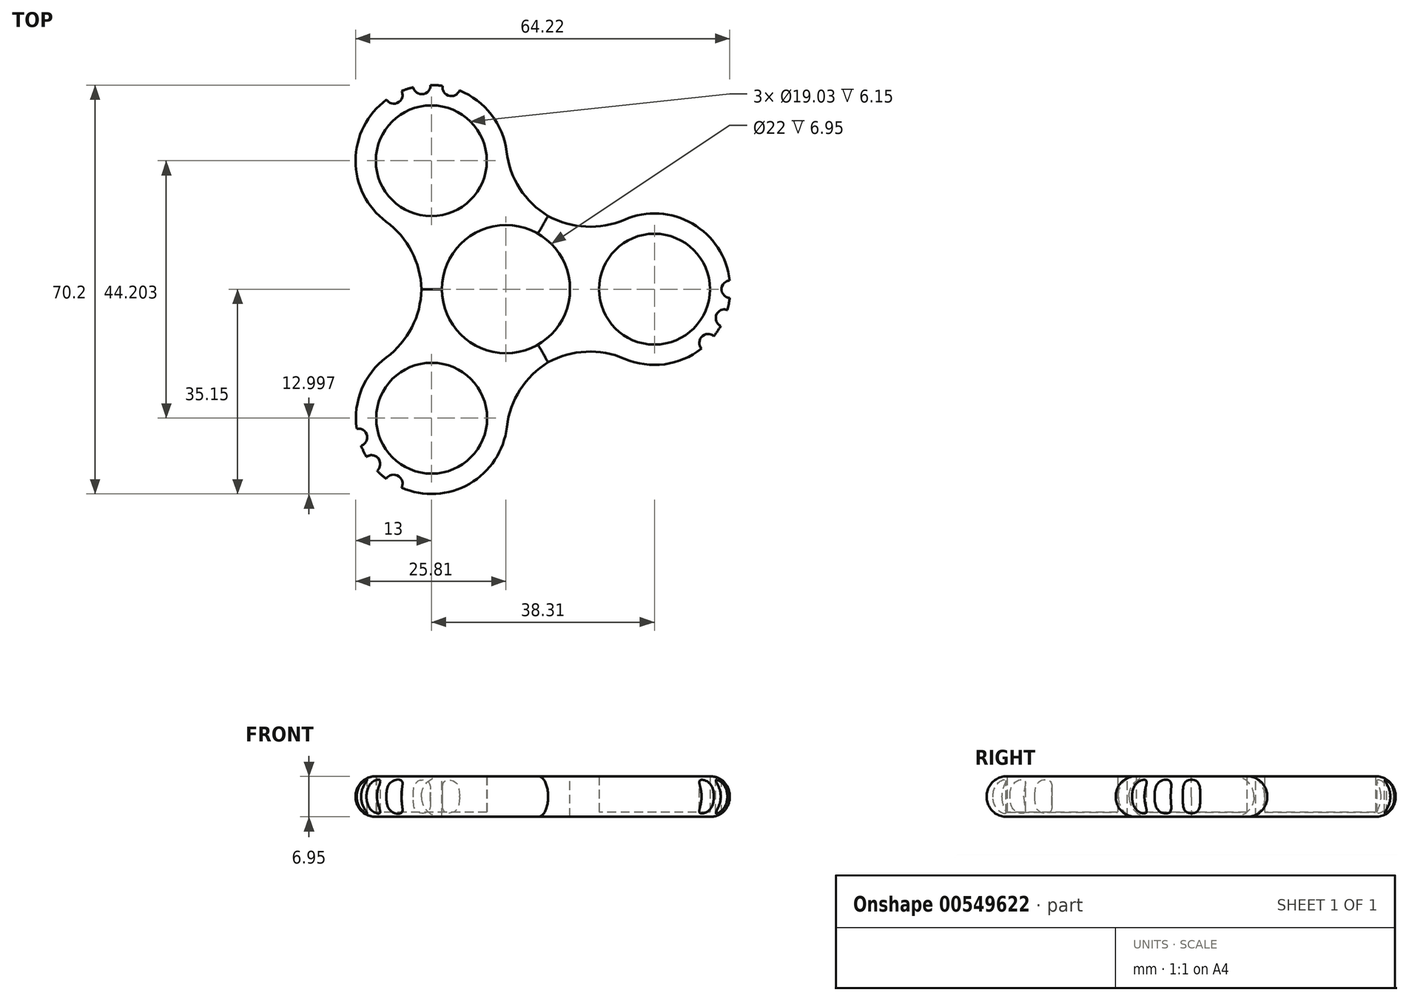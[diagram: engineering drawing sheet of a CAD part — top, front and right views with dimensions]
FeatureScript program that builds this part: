
annotation { "Feature Type Name" : "Feature", "Feature Type Description" : "" }
export const myFeature = defineFeature(function(context is Context, id is Id, definition is map)
    precondition{}
    {
        {
            var Q0;
            Q0=qCreatedBy(makeId("Top.planeOp"),FACE);
            var sketch = newSketch(context, id + "F0", { "sketchPlane" : qUnion([Q0])});
            skArc(sketch, "E0", {"start": v(13.56, -5.14) * mm, "mid": v(38.5, 0) * mm, "end": v(13.56, 5.14) * mm});
            skCircle(sketch, "E1", {"center": v(0, 0) * mm, "radius": 11 * mm});
            skCircle(sketch, "E2", {"center": v(25.5, 0) * mm, "radius": 9.52 * mm});
            skArc(sketch, "E3.1.1", {"start": v(-2.37, 14.3) * mm, "mid": v(-19.34, 33.3) * mm, "end": v(-11.25, 9.14) * mm});
            skCircle(sketch, "E3.1.2", {"center": v(-12.81, 22.05) * mm, "radius": 9.52 * mm});
            skArc(sketch, "E3.2.1", {"start": v(-11.17, -9.25) * mm, "mid": v(-19.24, -33.42) * mm, "end": v(-2.39, -14.3) * mm});
            skCircle(sketch, "E3.2.2", {"center": v(-12.75, -22.15) * mm, "radius": 9.52 * mm});
            skPoint(sketch, "E3.center", {"position": v(-0.02, -0.03) * mm});
            skArc(sketch, "E4", {"start": v(-11.25, 9.14) * mm, "mid": v(-14.5, -0.07) * mm, "end": v(-11.17, -9.25) * mm});
            skArc(sketch, "E5.trimOffspring", {"start": v(-2.39, -14.3) * mm, "mid": v(7.22, -12.57) * mm, "end": v(13.56, -5.14) * mm});
            skArc(sketch, "E6.trimOffspring", {"start": v(13.56, 5.14) * mm, "mid": v(7.23, 12.57) * mm, "end": v(-2.37, 14.3) * mm});
            skSolve(sketch);
        }
        {
            var Q0;
            Q0=makeQuery(id+"F0.imprint","IMPRINT",FACE,{"disambiguationData":[TD([[makeQuery(id+"F0.imprint","IMPRINT",EDGE,{"derivedFrom":sQuery(id+"F0.wireOp",EDGE,"E3.1.2")}),-1.0]])]});
            var Q1;
            {var subQ7=sQuery(id+"F0.wireOp",EDGE,"s7jpMl1W-r8wG-a5Qh-Sgcx-P4qn6cR7i1xz");var subQ8=sQuery(id+"F0.wireOp",EDGE,"E1");var subQ9=makeQuery(id+"F0.imprint","INTERSECT",VERTEX,{"derivedFrom":[subQ8,subQ7]});Q1=makeQuery(id+"F0.imprint","IMPRINT",FACE,{"disambiguationData":[TD([[makeQuery(id+"F0.imprint","IMPRINT",EDGE,{"disambiguationData":[TD([[subQ9,-1.0]])],"derivedFrom":subQ8}),-1.0]])]});}
            var Q2;
            {var subQ0=sQuery(id+"F0.wireOp",EDGE,"E1");var subQ4=makeQuery(id+"F0.imprint","INTERSECT",VERTEX,{"derivedFrom":[subQ0,sQuery(id+"F0.wireOp",EDGE,"s7jpMl1W-r8wG-a5Qh-Sgcx-P4qn6cR7i1xz")]});Q2=makeQuery(id+"F0.imprint","IMPRINT",FACE,{"disambiguationData":[TD([[makeQuery(id+"F0.imprint","IMPRINT",EDGE,{"disambiguationData":[TD([[subQ4,1.0]])],"derivedFrom":subQ0}),1.0]])]});}
            var Q3;
            {var subQ0=sQuery(id+"F0.wireOp",EDGE,"s7jpMl1W-r8wG-a5Qh-Sgcx-P4qn6cR7i1xz");var subQ1=sQuery(id+"F0.wireOp",EDGE,"E1");var subQ2=makeQuery(id+"F0.imprint","INTERSECT",VERTEX,{"derivedFrom":[subQ1,subQ0]});Q3=makeQuery(id+"F0.imprint","IMPRINT",FACE,{"disambiguationData":[TD([[makeQuery(id+"F0.imprint","IMPRINT",EDGE,{"disambiguationData":[TD([[subQ2,1.0]])],"derivedFrom":subQ1}),-1.0]])]});}
            var Q4;
            {var subQ1=sQuery(id+"F0.wireOp",EDGE,"E0");var subQ5=sQuery(id+"F0.wireOp",EDGE,"s7jpMl1W-r8wG-a5Qh-Sgcx-P4qn6cR7i1xz");var subQ6=makeQuery(id+"F0.imprint","INTERSECT",VERTEX,{"derivedFrom":[subQ1,subQ5]});Q4=makeQuery(id+"F0.imprint","IMPRINT",FACE,{"disambiguationData":[TD([[makeQuery(id+"F0.imprint","IMPRINT",EDGE,{"disambiguationData":[TD([[subQ6,-1.0]])],"derivedFrom":subQ1}),-1.0]])]});}
            var Q5;
            Q5=makeQuery(id+"F0.imprint","IMPRINT",FACE,{"disambiguationData":[TD([[makeQuery(id+"F0.imprint","IMPRINT",EDGE,{"derivedFrom":sQuery(id+"F0.wireOp",EDGE,"E2")}),-1.0]])]});
            var Q6;
            {var subQ0=sQuery(id+"F0.wireOp",EDGE,"E3.1.0");var subQ1=sQuery(id+"F0.wireOp",EDGE,"E1");var subQ2=makeQuery(id+"F0.imprint","INTERSECT",VERTEX,{"derivedFrom":[subQ1,subQ0]});Q6=makeQuery(id+"F0.imprint","IMPRINT",FACE,{"disambiguationData":[TD([[makeQuery(id+"F0.imprint","IMPRINT",EDGE,{"disambiguationData":[TD([[subQ2,1.0]])],"derivedFrom":subQ1}),-1.0]])]});}
            var Q7;
            {var subQ0=sQuery(id+"F0.wireOp",EDGE,"oMTgFF3v-ILPk-WRDk-ok4o-FcpdyRUbkfb3");var subQ1=sQuery(id+"F0.wireOp",EDGE,"E1");var subQ2=makeQuery(id+"F0.imprint","INTERSECT",VERTEX,{"derivedFrom":[subQ1,subQ0]});Q7=makeQuery(id+"F0.imprint","IMPRINT",FACE,{"disambiguationData":[TD([[makeQuery(id+"F0.imprint","IMPRINT",EDGE,{"disambiguationData":[TD([[subQ2,-1.0]])],"derivedFrom":subQ1}),-1.0]])]});}
            var Q8;
            {var subQ3=sQuery(id+"F0.wireOp",EDGE,"oMTgFF3v-ILPk-WRDk-ok4o-FcpdyRUbkfb3");var subQ5=sQuery(id+"F0.wireOp",EDGE,"E1");var subQ6=makeQuery(id+"F0.imprint","INTERSECT",VERTEX,{"derivedFrom":[subQ5,subQ3]});Q8=makeQuery(id+"F0.imprint","IMPRINT",FACE,{"disambiguationData":[TD([[makeQuery(id+"F0.imprint","IMPRINT",EDGE,{"disambiguationData":[TD([[subQ6,1.0]])],"derivedFrom":subQ5}),-1.0]])]});}
            var Q9;
            Q9=makeQuery(id+"F0.imprint","IMPRINT",FACE,{"disambiguationData":[TD([[makeQuery(id+"F0.imprint","IMPRINT",EDGE,{"derivedFrom":sQuery(id+"F0.wireOp",EDGE,"E3.2.2")}),-1.0]])]});
            extrude(context, id + "F1", {"entities" : qUnion([Q0, Q1, Q2, Q3, Q4, Q5, Q6, Q7, Q8, Q9]), "depth" : 6.95 * mm, "offsetDistance" : 25 * mm});
        }
        {
            var Q0;
            Q0=makeQuery(id+"F1.opExtrude","SWEPT_EDGE",EDGE,{"disambiguationData":[OSD([sQuery(id+"F0.wireOp",EDGE,"E3.1.1"),sQuery(id+"F0.wireOp",EDGE,"E4")])]});
            var Q1;
            Q1=makeQuery(id+"F1.opExtrude","SWEPT_EDGE",EDGE,{"disambiguationData":[OSD([sQuery(id+"F0.wireOp",EDGE,"E3.2.1"),sQuery(id+"F0.wireOp",EDGE,"E4")])]});
            var Q2;
            Q2=makeQuery(id+"F1.opExtrude","SWEPT_EDGE",EDGE,{"disambiguationData":[OSD([sQuery(id+"F0.wireOp",EDGE,"E0"),sQuery(id+"F0.wireOp",EDGE,"E5.trimOffspring")])]});
            var Q3;
            Q3=makeQuery(id+"F1.opExtrude","SWEPT_EDGE",EDGE,{"disambiguationData":[OSD([sQuery(id+"F0.wireOp",EDGE,"E3.2.1"),sQuery(id+"F0.wireOp",EDGE,"E5.trimOffspring")])]});
            var Q4;
            Q4=makeQuery(id+"F1.opExtrude","SWEPT_EDGE",EDGE,{"disambiguationData":[OSD([sQuery(id+"F0.wireOp",EDGE,"E0"),sQuery(id+"F0.wireOp",EDGE,"E6.trimOffspring")])]});
            var Q5;
            Q5=makeQuery(id+"F1.opExtrude","SWEPT_EDGE",EDGE,{"disambiguationData":[OSD([sQuery(id+"F0.wireOp",EDGE,"E3.1.1"),sQuery(id+"F0.wireOp",EDGE,"E6.trimOffspring")])]});
            fillet(context, id + "F2", {"entities" : qUnion([Q0, Q1, Q2, Q3, Q4, Q5]), "radius" : 15 * mm, "tangentPropagation" : true, "allowEdgeOverflow" : false});
        }
        {
            var Q0;
            {var subQ0=sQuery(id+"F0.wireOp",EDGE,"E6.trimOffspring");var subQ1=sQuery(id+"F0.wireOp",EDGE,"E3.1.1");Q0=makeQuery(id+"F2.opFillet","BLEND_EDGE",EDGE,{"blendedFrom":[makeQuery(id+"F1.opExtrude","SWEPT_EDGE",EDGE,{"disambiguationData":[OSD([subQ1,subQ0])]}),makeQuery(id+"F1.opExtrude","CAP_FACE",FACE,{"disambiguationData":[OSD([sQuery(id+"F0.wireOp",EDGE,"E0"),sQuery(id+"F0.wireOp",EDGE,"E1"),sQuery(id+"F0.wireOp",EDGE,"E2"),subQ1,sQuery(id+"F0.wireOp",EDGE,"E3.1.2"),sQuery(id+"F0.wireOp",EDGE,"E3.2.1"),sQuery(id+"F0.wireOp",EDGE,"E3.2.2"),sQuery(id+"F0.wireOp",EDGE,"E4"),sQuery(id+"F0.wireOp",EDGE,"E5.trimOffspring"),subQ0])],"isStart":false})],"blendedInto":[makeQuery(id+"F1.opExtrude","CAP_FACE",FACE,{"disambiguationData":[OSD([sQuery(id+"F0.wireOp",EDGE,"E0"),sQuery(id+"F0.wireOp",EDGE,"E1"),sQuery(id+"F0.wireOp",EDGE,"E2"),subQ1,sQuery(id+"F0.wireOp",EDGE,"E3.1.2"),sQuery(id+"F0.wireOp",EDGE,"E3.2.1"),sQuery(id+"F0.wireOp",EDGE,"E3.2.2"),sQuery(id+"F0.wireOp",EDGE,"E4"),sQuery(id+"F0.wireOp",EDGE,"E5.trimOffspring"),subQ0])],"isStart":false})]});}
            var Q1;
            Q1=makeQuery(id+"F1.opExtrude","CAP_EDGE",EDGE,{"disambiguationData":[OSD([sQuery(id+"F0.wireOp",EDGE,"E0")])],"isStart":false});
            var Q2;
            Q2=makeQuery(id+"F1.opExtrude","CAP_EDGE",EDGE,{"disambiguationData":[OSD([sQuery(id+"F0.wireOp",EDGE,"E3.2.1")])],"isStart":false});
            var Q3;
            {var subQ0=sQuery(id+"F0.wireOp",EDGE,"E6.trimOffspring");var subQ1=sQuery(id+"F0.wireOp",EDGE,"E3.1.1");Q3=makeQuery(id+"F2.opFillet","BLEND_EDGE",EDGE,{"blendedFrom":[makeQuery(id+"F1.opExtrude","SWEPT_EDGE",EDGE,{"disambiguationData":[OSD([subQ1,subQ0])]}),makeQuery(id+"F1.opExtrude","CAP_FACE",FACE,{"disambiguationData":[OSD([sQuery(id+"F0.wireOp",EDGE,"E0"),sQuery(id+"F0.wireOp",EDGE,"E1"),sQuery(id+"F0.wireOp",EDGE,"E2"),subQ1,sQuery(id+"F0.wireOp",EDGE,"E3.1.2"),sQuery(id+"F0.wireOp",EDGE,"E3.2.1"),sQuery(id+"F0.wireOp",EDGE,"E3.2.2"),sQuery(id+"F0.wireOp",EDGE,"E4"),sQuery(id+"F0.wireOp",EDGE,"E5.trimOffspring"),subQ0])],"isStart":true})],"blendedInto":[makeQuery(id+"F1.opExtrude","CAP_FACE",FACE,{"disambiguationData":[OSD([sQuery(id+"F0.wireOp",EDGE,"E0"),sQuery(id+"F0.wireOp",EDGE,"E1"),sQuery(id+"F0.wireOp",EDGE,"E2"),subQ1,sQuery(id+"F0.wireOp",EDGE,"E3.1.2"),sQuery(id+"F0.wireOp",EDGE,"E3.2.1"),sQuery(id+"F0.wireOp",EDGE,"E3.2.2"),sQuery(id+"F0.wireOp",EDGE,"E4"),sQuery(id+"F0.wireOp",EDGE,"E5.trimOffspring"),subQ0])],"isStart":true})]});}
            var Q4;
            Q4=makeQuery(id+"F1.opExtrude","CAP_EDGE",EDGE,{"disambiguationData":[OSD([sQuery(id+"F0.wireOp",EDGE,"E3.2.1")])],"isStart":true});
            var Q5;
            Q5=makeQuery(id+"F1.opExtrude","CAP_EDGE",EDGE,{"disambiguationData":[OSD([sQuery(id+"F0.wireOp",EDGE,"E0")])],"isStart":true});
            fillet(context, id + "F3", {"entities" : qUnion([Q0, Q1, Q2, Q3, Q4, Q5]), "radius" : 3.4 * mm, "tangentPropagation" : true, "allowEdgeOverflow" : false});
        }
        {
            var Q0;
            Q0=makeQuery(id+"F1.opExtrude","CAP_FACE",FACE,{"disambiguationData":[OSD([sQuery(id+"F0.wireOp",EDGE,"E0"),sQuery(id+"F0.wireOp",EDGE,"s7jpMl1W-r8wG-a5Qh-Sgcx-P4qn6cR7i1xz"),sQuery(id+"F0.wireOp",EDGE,"oMTgFF3v-ILPk-WRDk-ok4o-FcpdyRUbkfb3"),sQuery(id+"F0.wireOp",EDGE,"E2"),sQuery(id+"F0.wireOp",EDGE,"E3.1.0"),sQuery(id+"F0.wireOp",EDGE,"E3.1.1"),sQuery(id+"F0.wireOp",EDGE,"E3.1.2"),sQuery(id+"F0.wireOp",EDGE,"E3.1.3"),sQuery(id+"F0.wireOp",EDGE,"E3.2.0"),sQuery(id+"F0.wireOp",EDGE,"E3.2.1"),sQuery(id+"F0.wireOp",EDGE,"E3.2.2"),sQuery(id+"F0.wireOp",EDGE,"E3.2.3")])],"isStart":false});
            var sketch = newSketch(context, id + "F4", { "sketchPlane" : qUnion([Q0])});
            skCircle(sketch, "E7", {"center": v(0, 0) * mm, "radius": 11 * mm});
            skSolve(sketch);
        }
        {
            var Q0;
            Q0=makeQuery(id+"F4.imprint","IMPRINT",FACE,{"disambiguationData":[TD([[makeQuery(id+"F4.imprint","IMPRINT",EDGE,{"derivedFrom":sQuery(id+"F4.wireOp",EDGE,"E7")}),1.0]])]});
            extrude(context, id + "F5", {"entities" : qUnion([Q0]), "operationType" : NewBodyOperationType.REMOVE, "endBound" : BoundingType.THROUGH_ALL, "oppositeDirection" : true, "depth" : 25 * mm, "offsetDistance" : 25 * mm});
        }
        {
            var Q0;
            Q0=makeQuery(id+"F1.opExtrude","CAP_FACE",FACE,{"disambiguationData":[OSD([sQuery(id+"F0.wireOp",EDGE,"E0"),sQuery(id+"F0.wireOp",EDGE,"s7jpMl1W-r8wG-a5Qh-Sgcx-P4qn6cR7i1xz"),sQuery(id+"F0.wireOp",EDGE,"oMTgFF3v-ILPk-WRDk-ok4o-FcpdyRUbkfb3"),sQuery(id+"F0.wireOp",EDGE,"E2"),sQuery(id+"F0.wireOp",EDGE,"E3.1.0"),sQuery(id+"F0.wireOp",EDGE,"E3.1.1"),sQuery(id+"F0.wireOp",EDGE,"E3.1.2"),sQuery(id+"F0.wireOp",EDGE,"E3.1.3"),sQuery(id+"F0.wireOp",EDGE,"E3.2.0"),sQuery(id+"F0.wireOp",EDGE,"E3.2.1"),sQuery(id+"F0.wireOp",EDGE,"E3.2.2"),sQuery(id+"F0.wireOp",EDGE,"E3.2.3")])],"isStart":false});
            var sketch = newSketch(context, id + "F6", { "sketchPlane" : qUnion([Q0])});
            skCircle(sketch, "E8", {"center": v(38.5, 0) * mm, "radius": 1.5 * mm});
            skPoint(sketch, "E8.centerSnap0", {"position": v(35.1, 0) * mm});
            skCircle(sketch, "E9.1.0", {"center": v(37.52, -4.98) * mm, "radius": 1.5 * mm});
            skCircle(sketch, "E9.2.0", {"center": v(34.7, -9.2) * mm, "radius": 1.5 * mm});
            skPoint(sketch, "E9.center", {"position": v(25.5, 0) * mm});
            skLineSegment(sketch, "E9.anchor1", {"start": v(25.5, 0) * mm, "end": v(38.5, 0) * mm, "construction": true});
            skLineSegment(sketch, "E9.anchor2", {"start": v(25.5, 0) * mm, "end": v(34.7, -9.2) * mm, "construction": true});
            skCircle(sketch, "E10.MirrorC", {"center": v(37.52, 4.98) * mm, "radius": 1.5 * mm});
            skCircle(sketch, "E11.MirrorC", {"center": v(34.7, 9.2) * mm, "radius": 1.5 * mm});
            skCircle(sketch, "E12.1.0", {"center": v(-25.31, 25.45) * mm, "radius": 1.5 * mm});
            skCircle(sketch, "E12.1.1", {"center": v(-23.07, 30) * mm, "radius": 1.5 * mm});
            skCircle(sketch, "E12.1.2", {"center": v(-19.25, 33.35) * mm, "radius": 1.5 * mm});
            skCircle(sketch, "E12.1.3", {"center": v(-14.45, 34.98) * mm, "radius": 1.5 * mm});
            skCircle(sketch, "E12.1.4", {"center": v(-9.38, 34.65) * mm, "radius": 1.5 * mm});
            skCircle(sketch, "E12.2.0", {"center": v(-9.38, -34.65) * mm, "radius": 1.5 * mm});
            skCircle(sketch, "E12.2.1", {"center": v(-14.45, -34.98) * mm, "radius": 1.5 * mm});
            skCircle(sketch, "E12.2.2", {"center": v(-19.25, -33.35) * mm, "radius": 1.5 * mm});
            skCircle(sketch, "E12.2.3", {"center": v(-23.07, -30) * mm, "radius": 1.5 * mm});
            skCircle(sketch, "E12.2.4", {"center": v(-25.31, -25.45) * mm, "radius": 1.5 * mm});
            skPoint(sketch, "E12.center", {"position": v(0, 0) * mm});
            skSolve(sketch);
        }
        {
            var Q0;
            Q0=makeQuery(id+"F6.imprint","IMPRINT",FACE,{"disambiguationData":[TD([[makeQuery(id+"F6.imprint","IMPRINT",EDGE,{"derivedFrom":sQuery(id+"F6.wireOp",EDGE,"E11.MirrorC")}),-1.0]])]});
            var Q1;
            Q1=makeQuery(id+"F6.imprint","IMPRINT",FACE,{"disambiguationData":[TD([[makeQuery(id+"F6.imprint","IMPRINT",EDGE,{"derivedFrom":sQuery(id+"F6.wireOp",EDGE,"E10.MirrorC")}),-1.0]])]});
            var Q2;
            Q2=makeQuery(id+"F6.imprint","IMPRINT",FACE,{"disambiguationData":[TD([[makeQuery(id+"F6.imprint","IMPRINT",EDGE,{"derivedFrom":sQuery(id+"F6.wireOp",EDGE,"E8")}),1.0]])]});
            var Q3;
            Q3=makeQuery(id+"F6.imprint","IMPRINT",FACE,{"disambiguationData":[TD([[makeQuery(id+"F6.imprint","IMPRINT",EDGE,{"derivedFrom":sQuery(id+"F6.wireOp",EDGE,"E9.1.0")}),1.0]])]});
            var Q4;
            Q4=makeQuery(id+"F6.imprint","IMPRINT",FACE,{"disambiguationData":[TD([[makeQuery(id+"F6.imprint","IMPRINT",EDGE,{"derivedFrom":sQuery(id+"F6.wireOp",EDGE,"E9.2.0")}),1.0]])]});
            var Q5;
            Q5=makeQuery(id+"F6.imprint","IMPRINT",FACE,{"disambiguationData":[TD([[makeQuery(id+"F6.imprint","IMPRINT",EDGE,{"derivedFrom":sQuery(id+"F6.wireOp",EDGE,"E12.1.4")}),1.0]])]});
            var Q6;
            Q6=makeQuery(id+"F6.imprint","IMPRINT",FACE,{"disambiguationData":[TD([[makeQuery(id+"F6.imprint","IMPRINT",EDGE,{"derivedFrom":sQuery(id+"F6.wireOp",EDGE,"E12.1.3")}),1.0]])]});
            var Q7;
            Q7=makeQuery(id+"F6.imprint","IMPRINT",FACE,{"disambiguationData":[TD([[makeQuery(id+"F6.imprint","IMPRINT",EDGE,{"derivedFrom":sQuery(id+"F6.wireOp",EDGE,"E12.1.2")}),1.0]])]});
            var Q8;
            Q8=makeQuery(id+"F6.imprint","IMPRINT",FACE,{"disambiguationData":[TD([[makeQuery(id+"F6.imprint","IMPRINT",EDGE,{"derivedFrom":sQuery(id+"F6.wireOp",EDGE,"E12.1.1")}),-1.0]])]});
            var Q9;
            Q9=makeQuery(id+"F6.imprint","IMPRINT",FACE,{"disambiguationData":[TD([[makeQuery(id+"F6.imprint","IMPRINT",EDGE,{"derivedFrom":sQuery(id+"F6.wireOp",EDGE,"E12.1.0")}),-1.0]])]});
            var Q10;
            Q10=makeQuery(id+"F6.imprint","IMPRINT",FACE,{"disambiguationData":[TD([[makeQuery(id+"F6.imprint","IMPRINT",EDGE,{"derivedFrom":sQuery(id+"F6.wireOp",EDGE,"E12.2.4")}),1.0]])]});
            var Q11;
            Q11=makeQuery(id+"F6.imprint","IMPRINT",FACE,{"disambiguationData":[TD([[makeQuery(id+"F6.imprint","IMPRINT",EDGE,{"derivedFrom":sQuery(id+"F6.wireOp",EDGE,"E12.2.3")}),1.0]])]});
            var Q12;
            Q12=makeQuery(id+"F6.imprint","IMPRINT",FACE,{"disambiguationData":[TD([[makeQuery(id+"F6.imprint","IMPRINT",EDGE,{"derivedFrom":sQuery(id+"F6.wireOp",EDGE,"E12.2.2")}),1.0]])]});
            var Q13;
            Q13=makeQuery(id+"F6.imprint","IMPRINT",FACE,{"disambiguationData":[TD([[makeQuery(id+"F6.imprint","IMPRINT",EDGE,{"derivedFrom":sQuery(id+"F6.wireOp",EDGE,"E12.2.1")}),-1.0]])]});
            var Q14;
            Q14=makeQuery(id+"F6.imprint","IMPRINT",FACE,{"disambiguationData":[TD([[makeQuery(id+"F6.imprint","IMPRINT",EDGE,{"derivedFrom":sQuery(id+"F6.wireOp",EDGE,"E12.2.0")}),-1.0]])]});
            extrude(context, id + "F7", {"entities" : qUnion([Q0, Q1, Q2, Q3, Q4, Q5, Q6, Q7, Q8, Q9, Q10, Q11, Q12, Q13, Q14]), "operationType" : NewBodyOperationType.REMOVE, "endBound" : BoundingType.THROUGH_ALL, "oppositeDirection" : true, "depth" : 25 * mm, "offsetDistance" : 25 * mm});
        }
        {
            var Q0;
            Q0=makeQuery(id+"F1.opExtrude","CAP_FACE",FACE,{"disambiguationData":[OSD([sQuery(id+"F0.wireOp",EDGE,"E0"),sQuery(id+"F0.wireOp",EDGE,"E1"),sQuery(id+"F0.wireOp",EDGE,"E2"),sQuery(id+"F0.wireOp",EDGE,"E3.1.1"),sQuery(id+"F0.wireOp",EDGE,"E3.1.2"),sQuery(id+"F0.wireOp",EDGE,"E3.2.1"),sQuery(id+"F0.wireOp",EDGE,"E3.2.2"),sQuery(id+"F0.wireOp",EDGE,"E4"),sQuery(id+"F0.wireOp",EDGE,"E5.trimOffspring"),sQuery(id+"F0.wireOp",EDGE,"E6.trimOffspring")])],"isStart":true});
            var sketch = newSketch(context, id + "F8", { "sketchPlane" : qUnion([Q0])});
            skCircle(sketch, "E13.0", {"center": v(-12.75, 22.15) * mm, "radius": 9.52 * mm});
            skCircle(sketch, "E14.0", {"center": v(25.5, 0) * mm, "radius": 9.52 * mm});
            skCircle(sketch, "E15.0", {"center": v(-12.81, -22.05) * mm, "radius": 9.52 * mm});
            skSolve(sketch);
        }
        {
            var Q0;
            Q0=makeQuery(id+"F8.imprint","IMPRINT",FACE,{"disambiguationData":[TD([[makeQuery(id+"F8.imprint","IMPRINT",EDGE,{"derivedFrom":sQuery(id+"F8.wireOp",EDGE,"E13.0")}),-1.0]])]});
            var Q1;
            Q1=makeQuery(id+"F8.imprint","IMPRINT",FACE,{"disambiguationData":[TD([[makeQuery(id+"F8.imprint","IMPRINT",EDGE,{"derivedFrom":sQuery(id+"F8.wireOp",EDGE,"E14.0")}),-1.0]])]});
            var Q2;
            Q2=makeQuery(id+"F8.imprint","IMPRINT",FACE,{"disambiguationData":[TD([[makeQuery(id+"F8.imprint","IMPRINT",EDGE,{"derivedFrom":sQuery(id+"F8.wireOp",EDGE,"E15.0")}),-1.0]])]});
            extrude(context, id + "F9", {"entities" : qUnion([Q0, Q1, Q2]), "operationType" : NewBodyOperationType.ADD, "oppositeDirection" : true, "depth" : 0.8 * mm, "offsetDistance" : 25 * mm});
        }
    });
